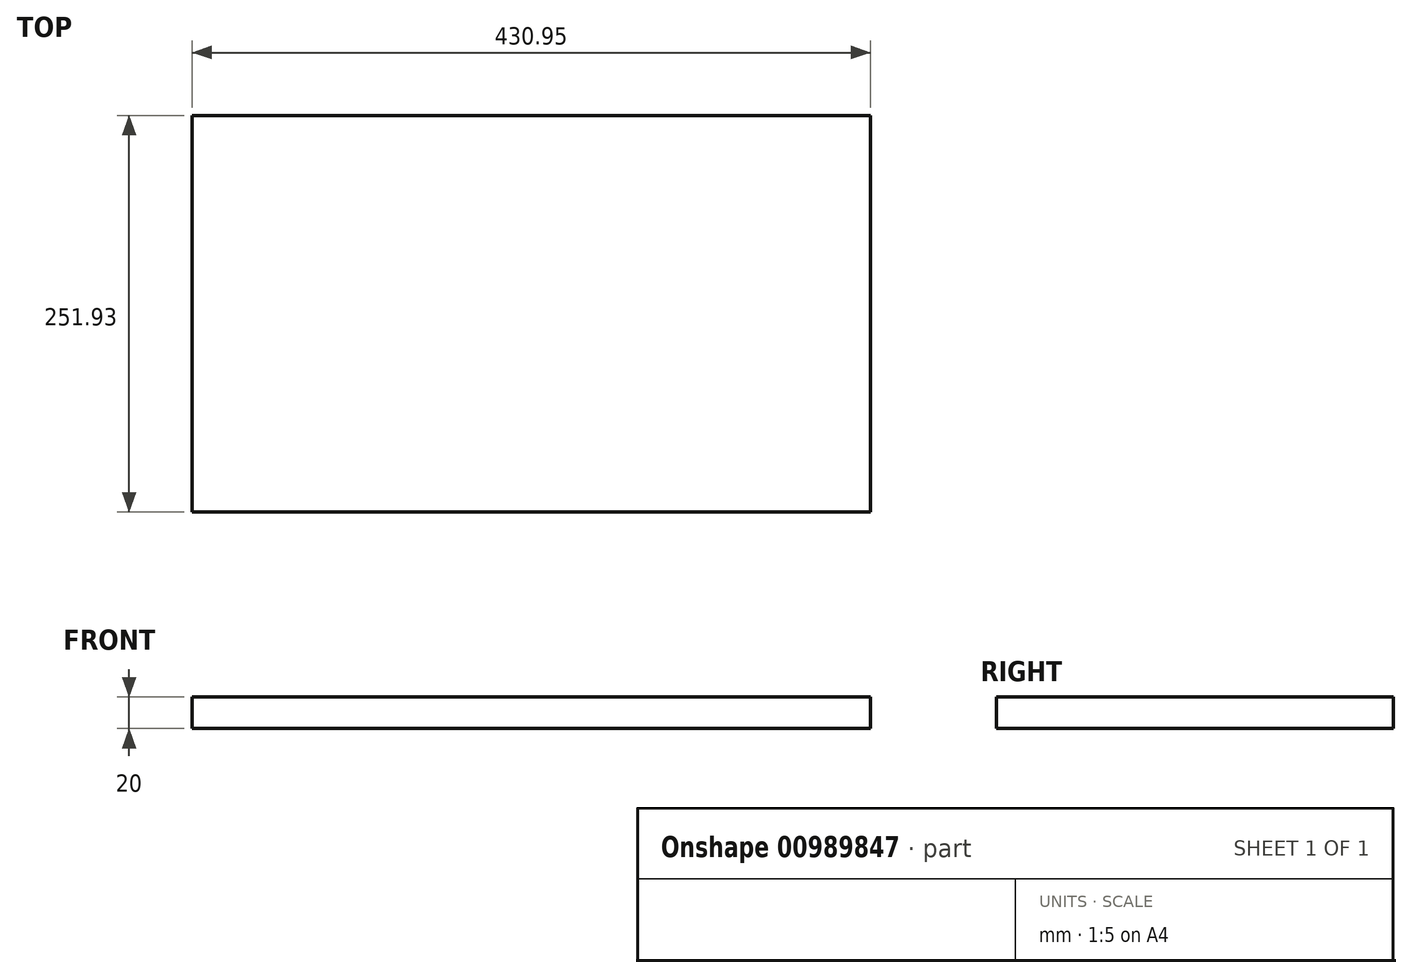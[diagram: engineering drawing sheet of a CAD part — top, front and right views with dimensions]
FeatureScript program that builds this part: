
annotation { "Feature Type Name" : "Feature", "Feature Type Description" : "" }
export const myFeature = defineFeature(function(context is Context, id is Id, definition is map)
    precondition{}
    {
        {
            var Q0;
            Q0=qCreatedBy(makeId("Top.planeOp"),FACE);
            var sketch = newSketch(context, id + "F0", { "sketchPlane" : qUnion([Q0])});
            skLineSegment(sketch, "E0.bottom", {"start": v(-201.54, -121.5) * mm, "end": v(229.4, -121.5) * mm});
            skLineSegment(sketch, "E0.top", {"start": v(-201.54, 130.44) * mm, "end": v(229.4, 130.44) * mm});
            skLineSegment(sketch, "E0.left", {"start": v(-201.54, -121.5) * mm, "end": v(-201.54, 130.44) * mm});
            skLineSegment(sketch, "E0.right", {"start": v(229.4, -121.5) * mm, "end": v(229.4, 130.44) * mm});
            skSolve(sketch);
        }
        {
            var Q0;
            Q0=makeQuery(id+"F0.imprint","IMPRINT",FACE,{"disambiguationData":[TD([[makeQuery(id+"F0.imprint","IMPRINT",EDGE,{"derivedFrom":sQuery(id+"F0.wireOp",EDGE,"E0.bottom")}),1.0]])]});
            extrude(context, id + "F1", {"entities" : qUnion([Q0]), "depth" : 20 * mm, "offsetDistance" : 25 * mm});
        }
    });
